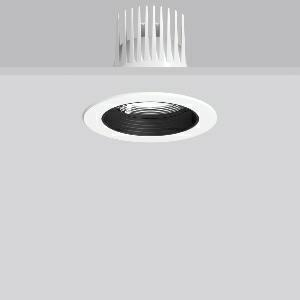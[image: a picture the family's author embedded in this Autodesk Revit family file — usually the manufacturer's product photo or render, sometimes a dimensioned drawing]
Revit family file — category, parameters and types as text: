
# Revit family: heledon_maxi_e_901767_002_1_69c5
name_source: partatom
category: Lighting Fixtures
units: mm (PartAtom-declared; Revit-internal decimal feet)

## family parameters
Cut with Voids When Loaded = No
Host = Face
Light Source = No
Part Type = Normal
Room Calculation Point = No
Round Connector Dimension = Use Diameter
Shared = No

## types (1)
- HELEDON maxi E (1 x LED Modul 940, 3900 lm, 4000)
    Apparent Load = 35 VA
    Approval mark = CE
    CIE Flux Codes = 97 100 100 100 100
    Color Rendering = 92
    Color Temperature = 4000
    Default Elevation = 1800 mm
    Description = Series: HELEDON maxi
Round recessed downlight. Housing: die-cast aluminium, powder-coated. Black plastic ring and recessed LED to prevent glare from the side. Optical assembly with lens made of plastic (polycarbonate) for the best homogeneous light distribution - can be changed without tools. Best colour rendering index Ra>90. Suitable for Recessed ceiling mounting. Installation without tools thanks to spring fastening system. Including separate LED converter with connecting cable 600 mm.High quality converter without flickering and stroboscopic effect. Through-wiring box (5 pole) available as accessory. The following accessories can be mounted without use of tools: interchangeable lenses, decorative glasses, honeycomb louvre, clear and frosted diffusers, white interchangeable plastic ring. 
Colour: traffic white, matt (RAL 9016)
Diameter: 162 mm
Height: 3 mm
Cut-out diameter: 152 mm
Recess height: 200 mm
Luminaire: recess height: 135 mm
Lamp: LED
Socket: without socket
Colour temperature: 4000K
Colour rendering index (CRI): 92
System power: 35 W
Rated luminous flux: 3900 lm
Luminous efficiency: 111 lm/W
Control gear: Regulated power supply
Protection class: II
Type of protection: IP 20
    Height = 0 mm  [stored 0 ft]
    Lamp = 1 x LED Modul 940
    Lamp Light Flux = 3900 lm
    Lamp count = 1
    Length = 162 mm
    Lifetime = 50000 h
    Luminous efficacy = 111 lm/W
    Manufacturer = RZB
    ModVariant = No
    Model = 901767.002.1
    Mounting Place = Ceiling
    Mounting Type = Recessed
    Number of Poles = 1
    OnlyDefault = Yes
    Power Factor = 1
    Product Name = HELEDON maxi E
    Product group = Recessed downlights
    ProductGroupID = 402
    Protection Class = Protection class II
    Protection Degree = IP 20
    RLX_Detail_Level = 1
    RLX_Emergency_Light_Flux = 0 lm
    RLX_Emergency_Type = 0
    RLX_Emergency_Type_DB = No
    RlxData = <blob elided: 119745 chars, md5=1cdcc698>
    Socket = socket
    Standby Power = 0 W
    System Light Flux = 3900 lm
    System Power = 35 W
    Type Comments = Product without accessories
    Type Image = 901663.002.jpg
    URL = http://relux.com
    VarID = ---
    Voltage = 230 V
    Voltage Range = 220-240 V
    Weight = 0.00 kg
    Width = 0 mm  [stored 0 ft]

note: [stored X ft] marks values corroborated as IEEE doubles in the binary element streams (Revit-internal decimal feet)

## geometry (parser evidence)
native form markers: Blend x4, Sweep x11
no freeform markers — native parametric forms only
